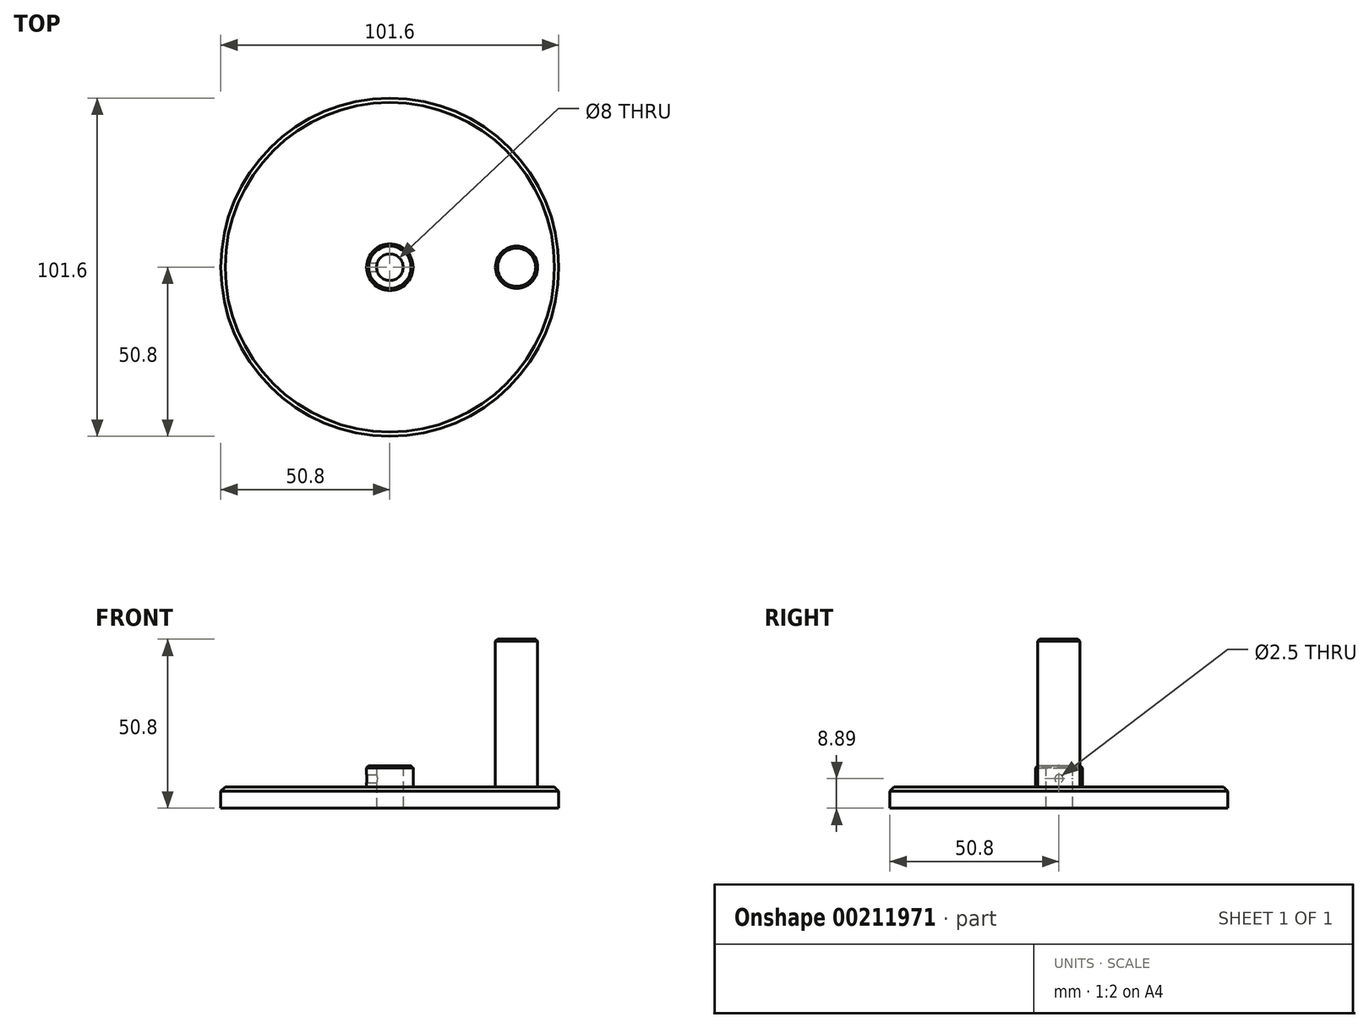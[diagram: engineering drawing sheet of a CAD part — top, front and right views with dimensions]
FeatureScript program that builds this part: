
annotation { "Feature Type Name" : "Feature", "Feature Type Description" : "" }
export const myFeature = defineFeature(function(context is Context, id is Id, definition is map)
    precondition{}
    {
        {
            var Q0;
            Q0=qCreatedBy(makeId("Top.planeOp"),FACE);
            var sketch = newSketch(context, id + "F0", { "sketchPlane" : qUnion([Q0])});
            skCircle(sketch, "E0", {"center": v(0, 0) * mm, "radius": 50.8 * mm});
            skCircle(sketch, "E1", {"center": v(0, 0) * mm, "radius": 7 * mm});
            skCircle(sketch, "E2", {"center": v(0, 0) * mm, "radius": 4 * mm});
            skCircle(sketch, "E3", {"center": v(38.1, 0) * mm, "radius": 6.35 * mm});
            skSolve(sketch);
        }
        {
            var Q0;
            Q0=makeQuery(id+"F0.imprint","IMPRINT",FACE,{"disambiguationData":[TD([[makeQuery(id+"F0.imprint","IMPRINT",EDGE,{"derivedFrom":sQuery(id+"F0.wireOp",EDGE,"E0")}),1.0]])]});
            extrude(context, id + "F1", {"entities" : qUnion([Q0]), "depth" : 6.35 * mm});
        }
        {
            var Q0;
            Q0=makeQuery(id+"F0.imprint","IMPRINT",FACE,{"disambiguationData":[TD([[makeQuery(id+"F0.imprint","IMPRINT",EDGE,{"derivedFrom":sQuery(id+"F0.wireOp",EDGE,"E3")}),1.0]])]});
            extrude(context, id + "F2", {"entities" : qUnion([Q0]), "operationType" : NewBodyOperationType.ADD, "depth" : 50.8 * mm});
        }
        {
            var Q0;
            Q0=makeQuery(id+"F0.imprint","IMPRINT",FACE,{"disambiguationData":[TD([[makeQuery(id+"F0.imprint","IMPRINT",EDGE,{"derivedFrom":sQuery(id+"F0.wireOp",EDGE,"E1")}),1.0]])]});
            var Q1;
            Q1=sQuery(id+"F0.wireOp",EDGE,"E1");
            var Q2;
            Q2=sQuery(id+"F0.wireOp",EDGE,"E2");
            extrude(context, id + "F3", {"entities" : qUnion([Q0]), "operationType" : NewBodyOperationType.ADD, "surfaceEntities" : qUnion([Q1, Q2]), "depth" : 12.7 * mm});
        }
        {
            var Q0;
            Q0=makeQuery(id+"F2.opExtrude","CAP_EDGE",EDGE,{"disambiguationData":[OSD([sQuery(id+"F0.wireOp",EDGE,"E3")])],"isStart":false});
            var Q1;
            Q1=makeQuery(id+"F3.opExtrude","CAP_EDGE",EDGE,{"disambiguationData":[OSD([sQuery(id+"F0.wireOp",EDGE,"E1")])],"isStart":false});
            chamfer(context, id + "F4", {"entities" : qUnion([Q0, Q1]), "width" : 0.64 * mm, "tangentPropagation" : true});
        }
        {
            var Q0;
            Q0=qCreatedBy(makeId("Right.planeOp"),FACE);
            var sketch = newSketch(context, id + "F5", { "sketchPlane" : qUnion([Q0])});
            skCircle(sketch, "E4", {"center": v(0, 8.9) * mm, "radius": 1.25 * mm});
            skSolve(sketch);
        }
        {
            var Q0;
            Q0=makeQuery(id+"F5.imprint","IMPRINT",FACE,{"disambiguationData":[TD([[makeQuery(id+"F5.imprint","IMPRINT",EDGE,{"derivedFrom":sQuery(id+"F5.wireOp",EDGE,"E4")}),1.0]])]});
            var Q1;
            Q1=sQuery(id+"F5.wireOp",EDGE,"E4");
            extrude(context, id + "F6", {"entities" : qUnion([Q0]), "operationType" : NewBodyOperationType.REMOVE, "surfaceEntities" : qUnion([Q1]), "oppositeDirection" : true, "depth" : 25.4 * mm});
        }
        {
            var Q0;
            Q0=makeQuery(id+"F1.opExtrude","CAP_EDGE",EDGE,{"disambiguationData":[OSD([sQuery(id+"F0.wireOp",EDGE,"E0")])],"isStart":false});
            chamfer(context, id + "F7", {"entities" : qUnion([Q0]), "width" : 1.27 * mm, "tangentPropagation" : true});
        }
    });
